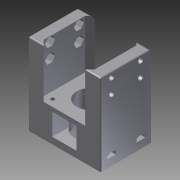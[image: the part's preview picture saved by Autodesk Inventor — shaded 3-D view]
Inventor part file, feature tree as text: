
AUTODESK INVENTOR PART (.ipt)
format: ipt  version: 2012 (Build 160160000, 160)  size: 432,640 bytes
history: native  units: mm
features: extrude x13, sketch x13, fillet x5, chamfer x1
ambient origin geometry x8: Origin, YZ Plane, XZ Plane, XY Plane, X Axis, Y Axis, Z Axis, Center Point
bodies: Solid1 (feature_tree)
feature tree (32):
  extrude  "Extrusion1"  Depth=42.4mm
  extrude  "Extrusion2"  Depth=3.1mm
  extrude  "Extrusion3"  Depth=31.0mm
  extrude  "Extrusion4"  Depth=42.4mm
  extrude  "Extrusion5"  Depth=4.0mm
  extrude  "Extrusion6"  Depth=4.0mm
  extrude  "Extrusion7"  Depth=4.0mm
  extrude  "Extrusion8"  Depth=4.0mm
  chamfer  "Chamfer1"  Distance=40.5mm
  fillet  "Fillet5"  Radius=4.2mm
  fillet  "Fillet3"  Radius=12.0mm
  fillet  "Fillet4"  Radius=12.0mm
  extrude  "Extrusion9"  Depth=9.2mm
  fillet  "Fillet6"  Radius=9.2mm
  extrude  "Extrusion10"  Depth=9.2mm
  fillet  "Fillet8"  Radius=9.2mm
  extrude  "Extrusion11"  Depth=7.1mm
  extrude  "Extrusion12"  Depth=7.2mm
  extrude  "Extrusion13"  Depth=3.5mm
  sketch  "Sketch1"  dims[d0=60.0mm d1=42.4mm]
  sketch  "Sketch2"  dims[d2=22.2mm d3=3.1mm]
  sketch  "Sketch3"  dims[d4=31.0mm d5=31.0mm]
  sketch  "Sketch4"  dims[d6=68.0mm d7=0.0mm d8=42.4mm]
  sketch  "Sketch5"  dims[d9=21.2mm d10=4.0mm]
  sketch  "Sketch6"  dims[d11=4.0mm d12=4.0mm]
  sketch  "Sketch7"  dims[d13=4.0mm d14=4.0mm]
  sketch  "Sketch8"  dims[d15=4.0mm d16=4.0mm]
  sketch  "Sketch9"  dims[d17=4.0mm d18=40.5mm d19=0.0mm d20=4.2mm d21=12.0mm d22=12.0mm]
  sketch  "Sketch10"  dims[d23=4.0mm d24=9.2mm d25=9.2mm]
  sketch  "Sketch11"  dims[d26=4.0mm d27=9.2mm d28=9.2mm]
  sketch  "Sketch12"  dims[d29=40.5mm d30=0.0mm d31=7.1mm]
  sketch  "Sketch13"  dims[d32=5.0mm d33=47.4mm d34=0.0mm d35=0.0mm d37=7.2mm d38=3.5mm d39=24.4mm d41=7.0mm d42=12.0mm d43=0.0mm d44=3.5mm d45=7.2mm d46=7.0mm d47=24.4mm d49=12.0mm d50=0.0mm d51=5.0mm d52=5.0mm d53=5.0mm d54=5.0mm d55=9.0mm d56=9.0mm d57=9.0mm d58=9.0mm d59=4.1mm d60=15.0mm d61=0.0mm d62=6.0mm d63=18.0mm d64=0.0mm d67=5.4mm d68=3.0mm d69=2.0mm d70=45.0deg d71=1.0mm d72=1.0mm d73=3.0mm d74=18.0mm d75=20.0mm d76=20.0mm d77=6.0mm d78=18.0mm d79=0.0mm d83=2.0mm d85=25.0mm d86=23.0mm d87=0.0mm d91=1.0mm d92=0.2mm d93=0.0mm d94=0.2mm d95=0.0mm d96=0.2mm d97=0.0mm d105=5.4mm]
